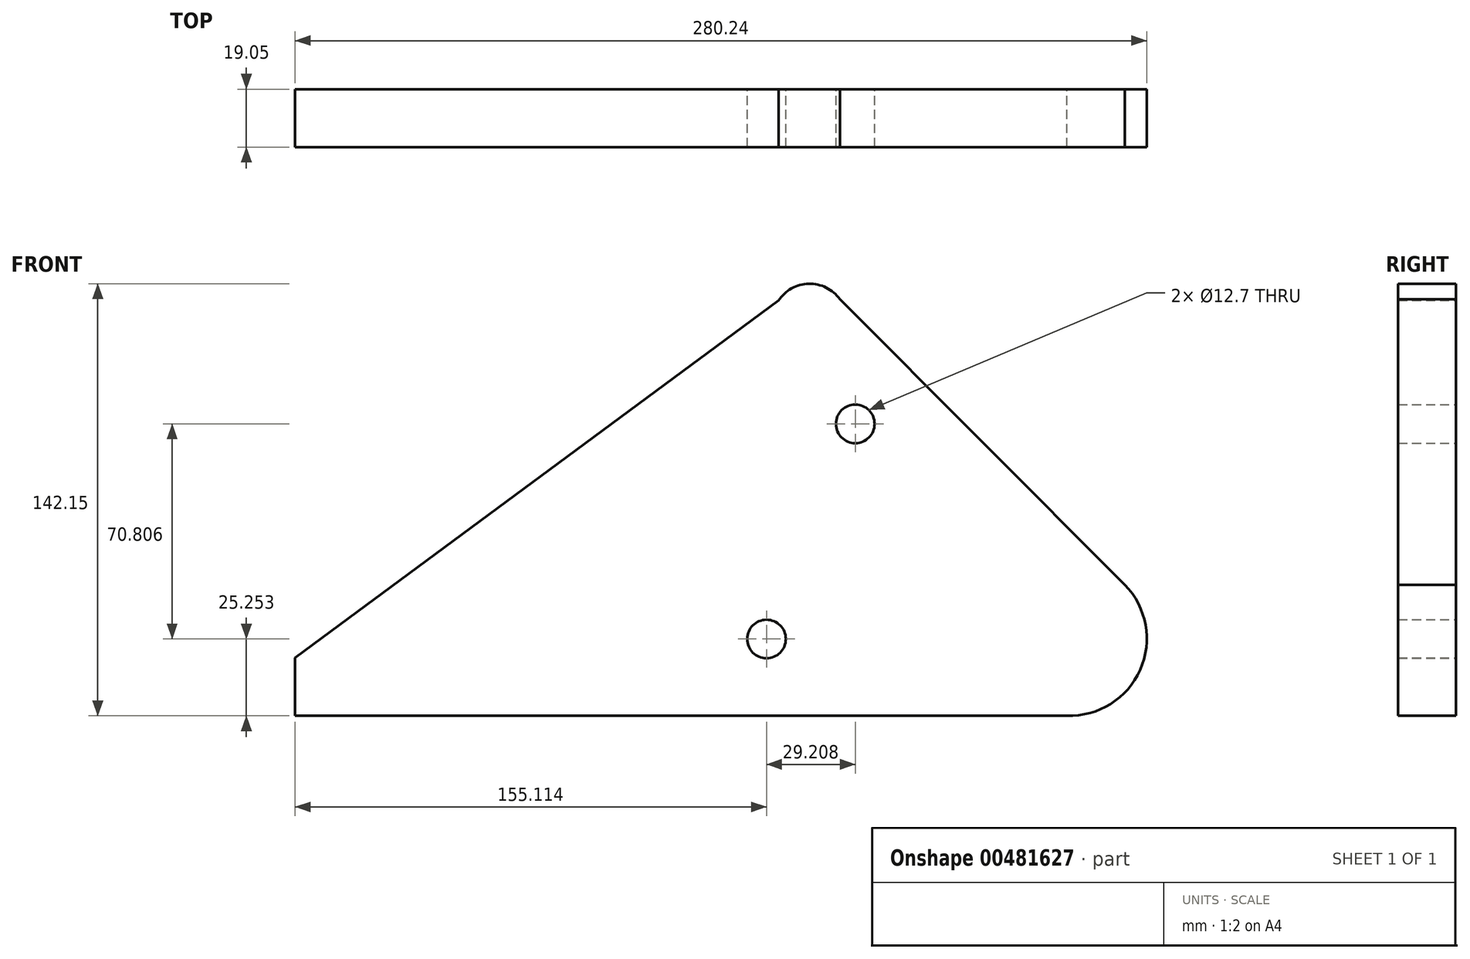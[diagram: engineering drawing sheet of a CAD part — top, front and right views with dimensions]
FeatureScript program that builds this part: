
annotation { "Feature Type Name" : "Feature", "Feature Type Description" : "" }
export const myFeature = defineFeature(function(context is Context, id is Id, definition is map)
    precondition{}
    {
        {
            var Q0;
            Q0=qCreatedBy(makeId("Front.planeOp"),FACE);
            var sketch = newSketch(context, id + "F0", { "sketchPlane" : qUnion([Q0])});
            skLineSegment(sketch, "E0", {"start": v(20.2, 111.84) * mm, "end": v(114.01, 17.85) * mm});
            skLineSegment(sketch, "E1", {"start": v(94.96, -25.24) * mm, "end": v(-159.04, -25.24) * mm});
            skLineSegment(sketch, "E2", {"start": v(-159.04, -25.24) * mm, "end": v(-159.04, -6.19) * mm});
            skLineSegment(sketch, "E3", {"start": v(-159.04, -6.19) * mm, "end": v(0, 111.36) * mm});
            skCircle(sketch, "E4", {"center": v(95.8, 0.14) * mm, "radius": 25.4 * mm});
            skPoint(sketch, "E4.third.point", {"position": v(70.41, 0) * mm});
            skCircle(sketch, "E5", {"center": v(10.27, 104.62) * mm, "radius": 12.29 * mm});
            skPoint(sketch, "E5.third.point", {"position": v(13.63, 92.8) * mm});
            skCircle(sketch, "E6", {"center": v(25.28, 70.8) * mm, "radius": 6.35 * mm});
            skCircle(sketch, "E7", {"center": v(-3.93, 0) * mm, "radius": 6.35 * mm});
            skArc(sketch, "E8", {"start": v(20.12, 74.5) * mm, "mid": v(0.96, 38.79) * mm, "end": v(-10.8, 0) * mm});
            skArc(sketch, "E9", {"start": v(31.14, 68.35) * mm, "mid": v(14.46, 35.15) * mm, "end": v(2.42, 0) * mm});
            skSolve(sketch);
        }
        {
            var Q0;
            {var subQ12=sQuery(id+"F0.wireOp",EDGE,"E1");Q0=makeQuery(id+"F0.imprint","IMPRINT",FACE,{"disambiguationData":[TD([[makeQuery(id+"F0.imprint","IMPRINT",EDGE,{"derivedFrom":subQ12}),-1.0]])]});}
            var Q1;
            {var subQ0=sQuery(id+"F0.wireOp",EDGE,"E4");var subQ1=sQuery(id+"F0.wireOp",EDGE,"E0");var subQ2=makeQuery(id+"F0.imprint","INTERSECT",VERTEX,{"disambiguationData":[OD(0.0)],"derivedFrom":[subQ1,subQ0]});Q1=makeQuery(id+"F0.imprint","IMPRINT",FACE,{"disambiguationData":[TD([[makeQuery(id+"F0.imprint","IMPRINT",EDGE,{"disambiguationData":[TD([[subQ2,1.0]])],"derivedFrom":subQ1}),-1.0]])]});}
            var Q2;
            {var subQ0=sQuery(id+"F0.wireOp",EDGE,"E5");var subQ1=makeQuery(id+"F0.imprint","INTERSECT",VERTEX,{"derivedFrom":[sQuery(id+"F0.wireOp",EDGE,"E0"),subQ0]});Q2=makeQuery(id+"F0.imprint","IMPRINT",FACE,{"disambiguationData":[TD([[makeQuery(id+"F0.imprint","IMPRINT",EDGE,{"disambiguationData":[TD([[subQ1,-1.0]])],"derivedFrom":subQ0}),1.0]])]});}
            extrude(context, id + "F1", {"entities" : qUnion([Q0, Q1, Q2]), "depth" : 19.05 * mm});
        }
    });
